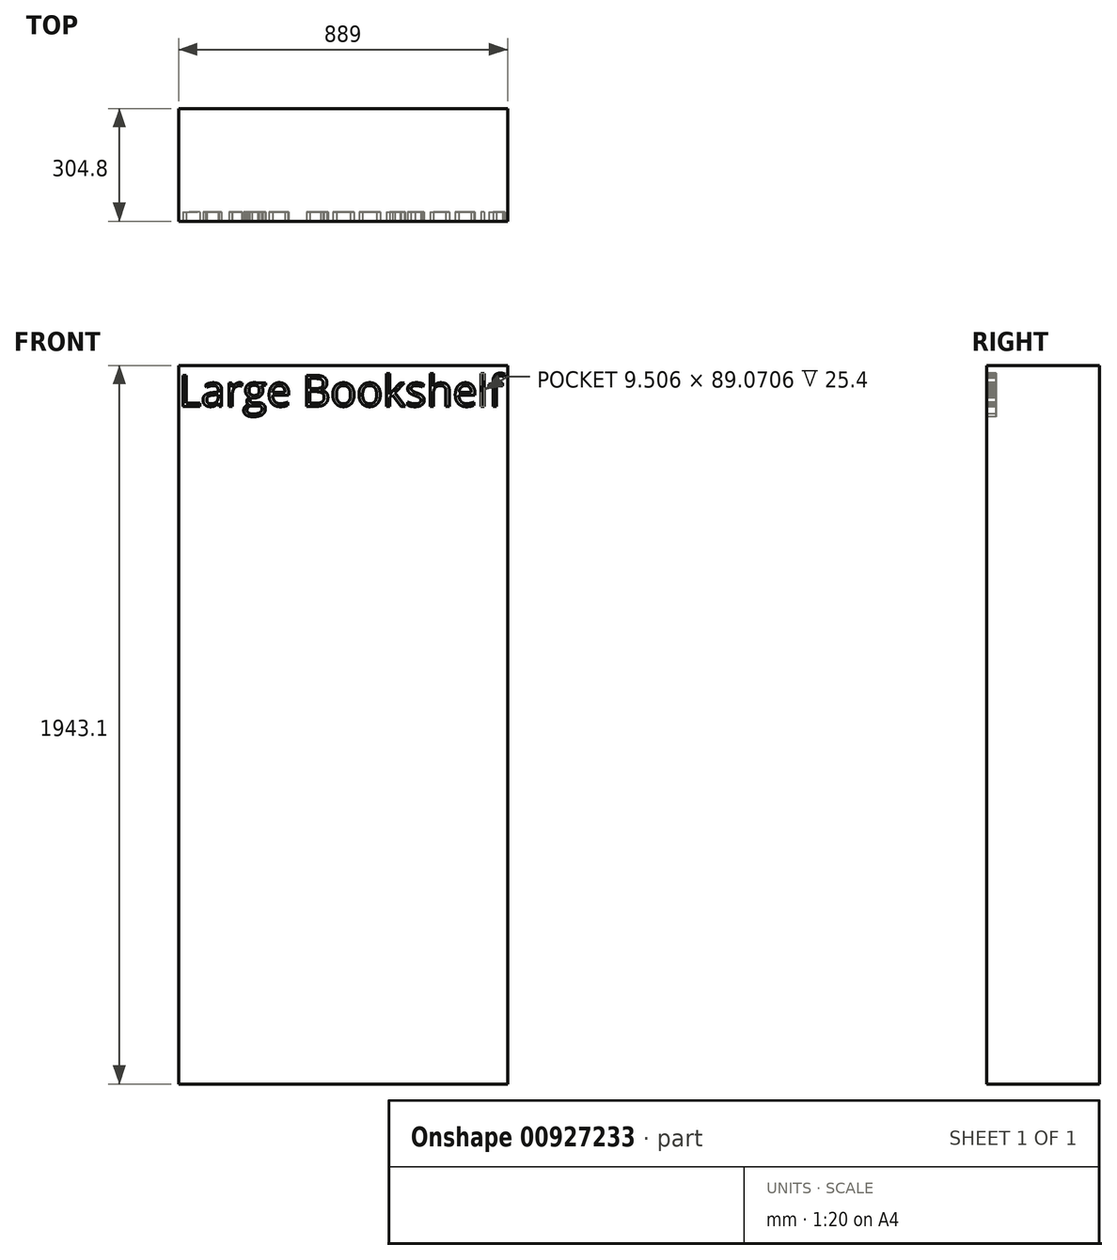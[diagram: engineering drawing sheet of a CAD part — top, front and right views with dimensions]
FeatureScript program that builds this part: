
annotation { "Feature Type Name" : "Feature", "Feature Type Description" : "" }
export const myFeature = defineFeature(function(context is Context, id is Id, definition is map)
    precondition{}
    {
        {
            var Q0;
            Q0=qCreatedBy(makeId("Front.planeOp"),FACE);
            var sketch = newSketch(context, id + "F0", { "sketchPlane" : qUnion([Q0])});
            skLineSegment(sketch, "E0.bottom", {"start": v(444.5, -971.55) * mm, "end": v(-444.5, -971.55) * mm});
            skLineSegment(sketch, "E0.top", {"start": v(444.5, 971.55) * mm, "end": v(-444.5, 971.55) * mm});
            skLineSegment(sketch, "E0.left", {"start": v(444.5, -971.55) * mm, "end": v(444.5, 971.55) * mm});
            skLineSegment(sketch, "E0.right", {"start": v(-444.5, -971.55) * mm, "end": v(-444.5, 971.55) * mm});
            skPoint(sketch, "E0.middle", {"position": v(0, 0) * mm});
            skSolve(sketch);
        }
        {
            var Q0;
            Q0 = qSketchRegion(id + "F0", true);
            extrude(context, id + "F1", {"entities" : qUnion([Q0]), "endBound" : BoundingType.SYMMETRIC, "depth" : 304.8 * mm, "offsetDistance" : 25.4 * mm});
        }
        {
            var Q0;
            Q0=makeQuery(id+"F1.opExtrude","CAP_FACE",FACE,{"disambiguationData":[OSD([sQuery(id+"F0.wireOp",EDGE,"E0.bottom"),sQuery(id+"F0.wireOp",EDGE,"E0.top"),sQuery(id+"F0.wireOp",EDGE,"E0.left"),sQuery(id+"F0.wireOp",EDGE,"E0.right")])],"isStart":false});
            var sketch = newSketch(context, id + "F2", { "sketchPlane" : qUnion([Q0])});
            skText(sketch, "E1", { "text": "Large Bookshelf", "fontName": "OpenSans-Regular.ttf"});
            const initialGuessF2  = {"E1": [-0.4445, 0.86099, 1, 0, 0.0844]};
            skSetInitialGuess(sketch, initialGuessF2);
            skSolve(sketch);
        }
        {
            var Q0;
            Q0 = qSketchRegion(id + "F2", true);
            extrude(context, id + "F3", {"entities" : qUnion([Q0]), "operationType" : NewBodyOperationType.REMOVE, "oppositeDirection" : true, "depth" : 25.4 * mm, "offsetDistance" : 25.4 * mm});
        }
    });
